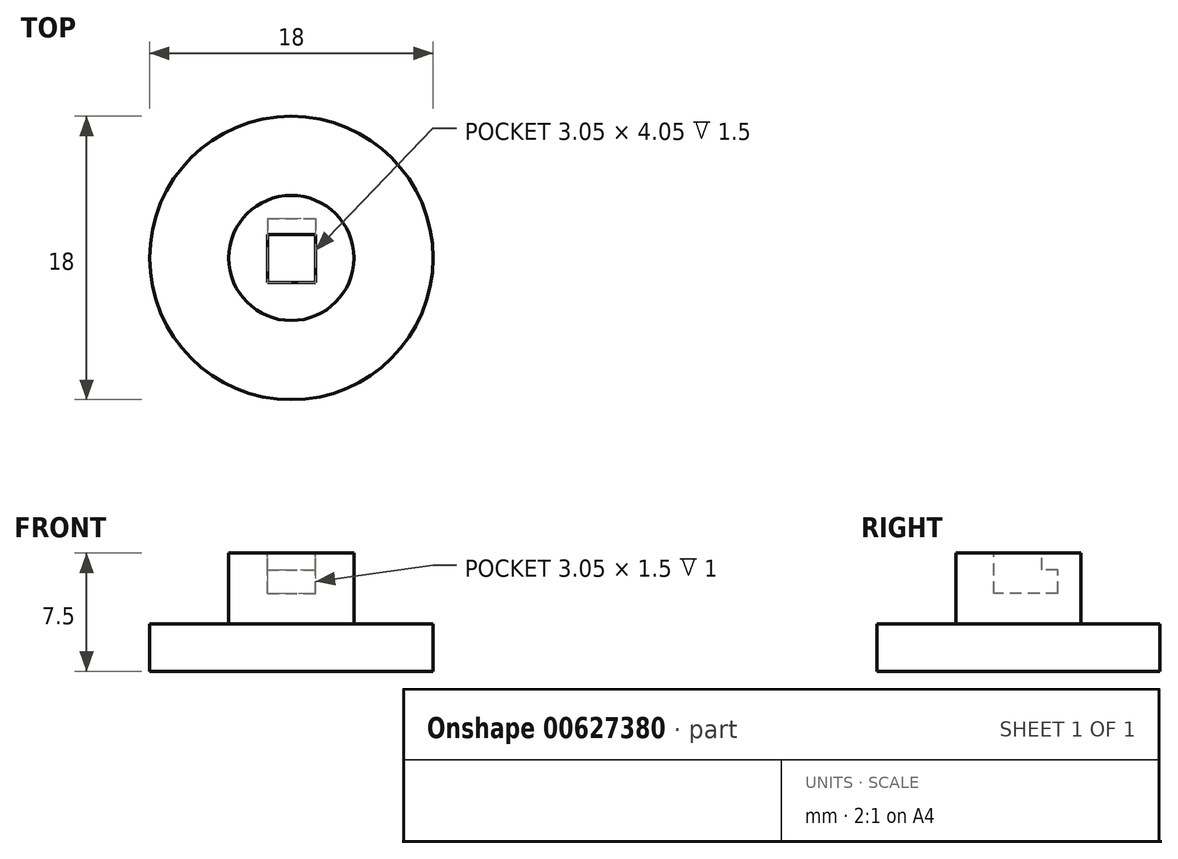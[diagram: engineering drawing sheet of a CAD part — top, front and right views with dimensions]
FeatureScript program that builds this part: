
annotation { "Feature Type Name" : "Feature", "Feature Type Description" : "" }
export const myFeature = defineFeature(function(context is Context, id is Id, definition is map)
    precondition{}
    {
        {
            var Q0;
            Q0=qCreatedBy(makeId("Top.planeOp"),FACE);
            var sketch = newSketch(context, id + "F0", { "sketchPlane" : qUnion([Q0])});
            skCircle(sketch, "E0", {"center": v(0, 0) * mm, "radius": 9 * mm});
            skSolve(sketch);
        }
        {
            var Q0;
            Q0=makeQuery(id+"F0.imprint","IMPRINT",FACE,{"disambiguationData":[TD([[makeQuery(id+"F0.imprint","IMPRINT",EDGE,{"derivedFrom":sQuery(id+"F0.wireOp",EDGE,"E0")}),1.0]])]});
            extrude(context, id + "F1", {"entities" : qUnion([Q0]), "depth" : 3 * mm, "offsetDistance" : 25 * mm});
        }
        {
            var Q0;
            Q0=makeQuery(id+"F1.opExtrude","CAP_FACE",FACE,{"disambiguationData":[OSD([sQuery(id+"F0.wireOp",EDGE,"E0")])],"isStart":false});
            var sketch = newSketch(context, id + "F2", { "sketchPlane" : qUnion([Q0])});
            skCircle(sketch, "E1", {"center": v(0, 0) * mm, "radius": 3.98 * mm});
            skSolve(sketch);
        }
        {
            var Q0;
            Q0 = qSketchRegion(id + "F2", true);
            extrude(context, id + "F3", {"entities" : qUnion([Q0]), "operationType" : NewBodyOperationType.ADD, "depth" : 4.5 * mm, "offsetDistance" : 25 * mm});
        }
        {
            var Q0;
            Q0=makeQuery(id+"F3.opExtrude","CAP_FACE",FACE,{"disambiguationData":[OSD([sQuery(id+"F2.wireOp",EDGE,"E1")])],"isStart":false});
            var sketch = newSketch(context, id + "F4", { "sketchPlane" : qUnion([Q0])});
            skLineSegment(sketch, "E2.bottom", {"start": v(-1.53, 1.5) * mm, "end": v(1.52, 1.5) * mm});
            skLineSegment(sketch, "E2.top", {"start": v(-1.52, -1.55) * mm, "end": v(1.52, -1.55) * mm});
            skLineSegment(sketch, "E2.left", {"start": v(-1.53, 1.5) * mm, "end": v(-1.52, -1.55) * mm});
            skLineSegment(sketch, "E2.right", {"start": v(1.52, 1.5) * mm, "end": v(1.52, -1.55) * mm});
            skSolve(sketch);
        }
        {
            var Q0;
            Q0 = qSketchRegion(id + "F4", true);
            extrude(context, id + "F5", {"entities" : qUnion([Q0]), "operationType" : NewBodyOperationType.REMOVE, "oppositeDirection" : true, "depth" : 2.55 * mm, "offsetDistance" : 25 * mm});
        }
        {
            var Q0;
            Q0=makeQuery(id+"F5.boolean.opBoolean","COPY",FACE,{"derivedFrom":makeQuery(id+"F5.opExtrude","SWEPT_FACE",FACE,{"disambiguationData":[OSD([sQuery(id+"F4.wireOp",EDGE,"E2.bottom")])]})});
            var sketch = newSketch(context, id + "F6", { "sketchPlane" : qUnion([Q0])});
            skLineSegment(sketch, "E3.bottom", {"start": v(-1.53, 4.95) * mm, "end": v(1.52, 4.95) * mm});
            skLineSegment(sketch, "E3.top", {"start": v(-1.53, 6.45) * mm, "end": v(1.52, 6.45) * mm});
            skLineSegment(sketch, "E3.left", {"start": v(-1.53, 4.95) * mm, "end": v(-1.53, 6.45) * mm});
            skLineSegment(sketch, "E3.right", {"start": v(1.52, 4.95) * mm, "end": v(1.52, 6.45) * mm});
            skSolve(sketch);
        }
        {
            var Q0;
            Q0 = qSketchRegion(id + "F6", true);
            extrude(context, id + "F7", {"entities" : qUnion([Q0]), "operationType" : NewBodyOperationType.REMOVE, "oppositeDirection" : true, "depth" : 1 * mm, "offsetDistance" : 25 * mm});
        }
    });
